# Revit family: Sanitary_Wash-Basins_HIMACS_HIMACS-Bowl-CB-3835
name_source: partatom
category: Plumbing Fixtures
revit_build: Autodesk Revit 2018 (Build: 20190510_1515(x64)
units: mm (PartAtom-declared; Revit-internal decimal feet)

## family parameters
Always vertical = No
Cut with Voids When Loaded = No
OmniClass Number = 23.31.13.00
OmniClass Title = Sinks
Part Type = Normal
Room Calculation Point = No
Round Connector Dimension = Use Diameter
Shared = No
Work Plane-Based = Yes

## types (1)
- HIMACS Bowl CB 3835
    Always visible = Yes
    BIMobject category = Wash Basins
    Default Elevation = 1219.2 mm  [stored 4 ft]
    Description = HIMACS Bowls offer superb ease of cleaning and a warm and pleasant feel, making them the ideal solution for creating the bathroom of your dreams. They are manufactured using a casting process and ideally suited for top mounted installation
    Design country = Spain
    Diameter = 45 mm  [stored 0.147638 ft]
    Edition number = 1
    IFC Classification = Furnishing Element
    Main material = HIMACS - Ceramic - Alpine White
    Manufacturer = HIMACS
    Manufacturer country = Spain
    Manufacturer name = HIMACS
    Material main = Solid surface
    Material secondary = Natural Acrylic Stone
    Model = HIMACS Bowl CB 3835
    NBS Reference Code = 35-65-70-94
    NBS Reference Description = Wash Basin Systems
    Product Guid = 6a7fdf28-46c0-41c3-b246-6b6439b72d98
    Product SKU = CB3835
    Product certification = http://himacs.eu
    Product data url = https://bimobject.com
    Product family = Sinks, Baby Baths & Bowls
    Product group = Bowls
    Product name = HIMACS Bowl CB 3835
    QR code = https://bimobject.com
    UNSPSC Code = 301815
    URL = https://himacs.eu
    Uniclass 1.4 Code = L7212
    Uniclass 1.4 Description = Washbasins
    Uniclass 2.0 Code = SS-35-65-70-94
    Uniclass 2.0 Description = Wash Basin Systems
    Weight Net (Kg) = 3,75

note: [stored X ft] marks values corroborated as IEEE doubles in the binary element streams (Revit-internal decimal feet)

## geometry (parser evidence)
native form markers: Sweep x4
no freeform markers — native parametric forms only
